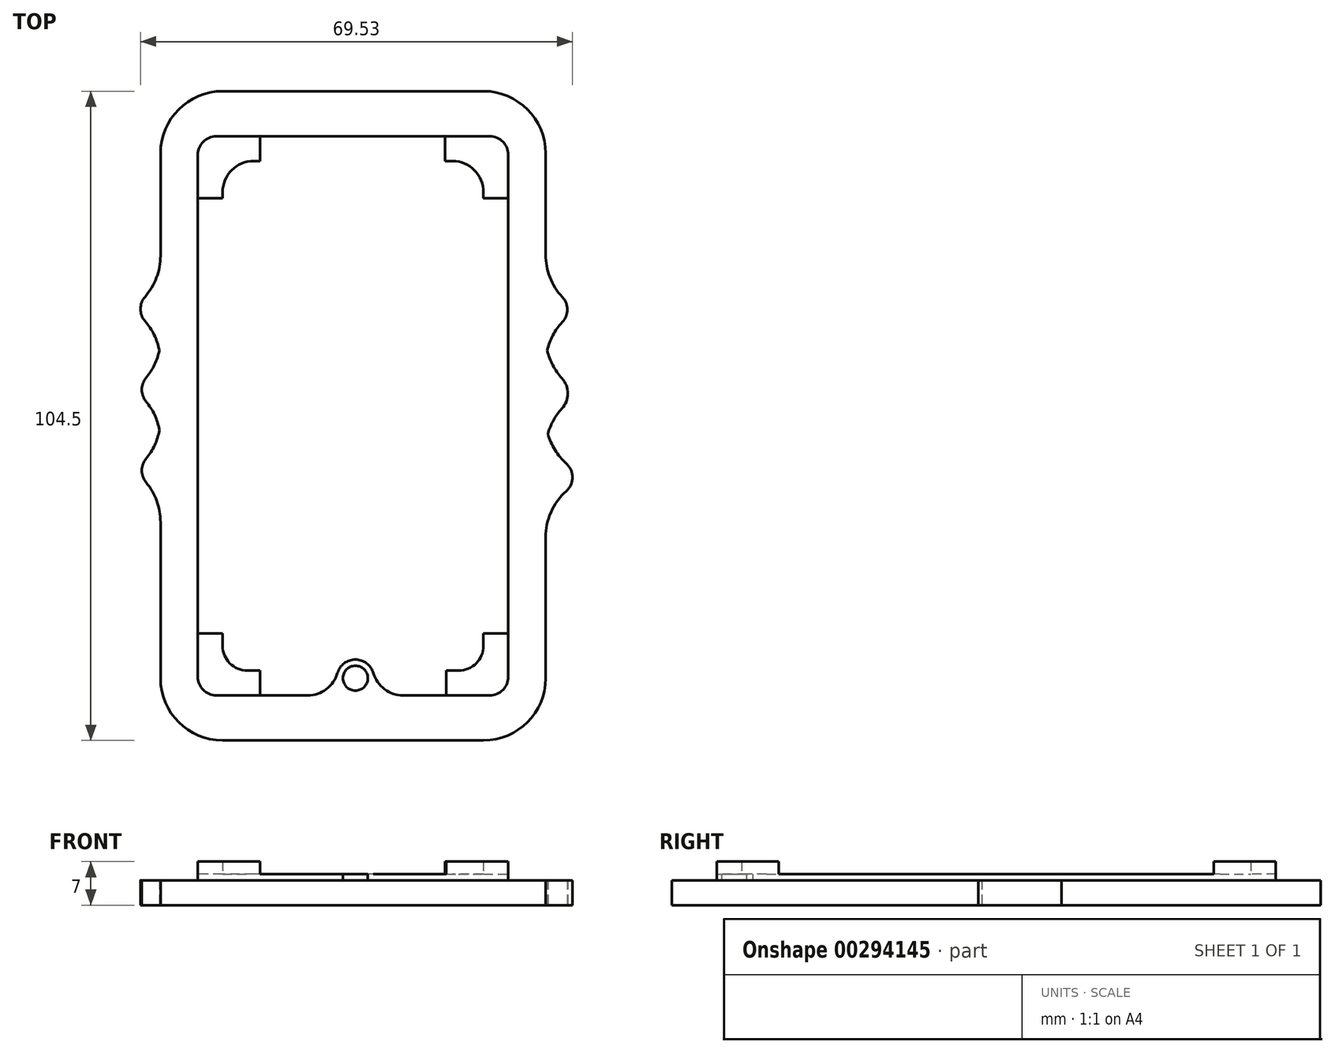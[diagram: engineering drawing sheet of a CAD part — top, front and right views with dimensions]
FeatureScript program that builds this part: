
annotation { "Feature Type Name" : "Feature", "Feature Type Description" : "" }
export const myFeature = defineFeature(function(context is Context, id is Id, definition is map)
    precondition{}
    {
        {
            var Q0;
            Q0=qCreatedBy(makeId("Top.planeOp"),FACE);
            var sketch = newSketch(context, id + "F0", { "sketchPlane" : qUnion([Q0])});
            skLineSegment(sketch, "E0.bottom", {"start": v(-9.13, 37.8) * mm, "end": v(20.7, 37.8) * mm});
            skLineSegment(sketch, "E0.top", {"start": v(-9.13, -52.2) * mm, "end": v(-1.43, -52.2) * mm});
            skLineSegment(sketch, "E0.left", {"start": v(-19.13, 27.8) * mm, "end": v(-19.13, -42.2) * mm});
            skLineSegment(sketch, "E0.right", {"start": v(30.87, 27.8) * mm, "end": v(30.87, -42.2) * mm});
            skPoint(sketch, "E1.end.orphan", {"position": v(5.87, -52.2) * mm});
            skPoint(sketch, "E1.start.orphan", {"position": v(5.87, 37.8) * mm});
            skPoint(sketch, "E2.visualSharp", {"position": v(30.87, 37.8) * mm});
            skPoint(sketch, "E3.visualSharp", {"position": v(-19.13, 37.8) * mm});
            skPoint(sketch, "E4.visualSharp", {"position": v(30.87, -52.2) * mm});
            skPoint(sketch, "E5.visualSharp", {"position": v(-19.13, -52.2) * mm});
            skArc(sketch, "E6", {"start": v(9.14, -48.6) * mm, "mid": v(6.25, -46.42) * mm, "end": v(3.37, -48.6) * mm});
            skLineSegment(sketch, "E7.trimOffspring", {"start": v(13.94, -52.2) * mm, "end": v(20.87, -52.2) * mm});
            skPoint(sketch, "E8", {"position": v(5.87, -46.45) * mm});
            skPoint(sketch, "E9.visualSharp", {"position": v(5.12, -52.2) * mm});
            skArc(sketch, "E9.filletArc", {"start": v(-1.43, -52.2) * mm, "mid": v(1.57, -51.2) * mm, "end": v(3.37, -48.6) * mm});
            skPoint(sketch, "E10.visualSharp", {"position": v(7.38, -52.2) * mm});
            skArc(sketch, "E10.filletArc", {"start": v(9.14, -48.6) * mm, "mid": v(10.93, -51.2) * mm, "end": v(13.94, -52.2) * mm});
            skPoint(sketch, "E11", {"position": v(-19.13, -7.2) * mm});
            skLineSegment(sketch, "E12.bottom", {"start": v(26.87, -59.45) * mm, "end": v(-15.13, -59.45) * mm});
            skLineSegment(sketch, "E12.top", {"start": v(26.87, 45.05) * mm, "end": v(-15.13, 45.05) * mm});
            skLineSegment(sketch, "E12.left", {"start": v(36.87, -49.45) * mm, "end": v(36.87, -26.78) * mm});
            skLineSegment(sketch, "E12.right", {"start": v(-25.13, -49.45) * mm, "end": v(-25.13, -24.3) * mm});
            skPoint(sketch, "E12.middle", {"position": v(5.87, -7.2) * mm});
            skPoint(sketch, "E13.visualSharp", {"position": v(-25.13, 45.05) * mm});
            skArc(sketch, "E13.filletArc", {"start": v(-15.13, 45.05) * mm, "mid": v(-22.2, 42.12) * mm, "end": v(-25.13, 35.05) * mm});
            skPoint(sketch, "E14.visualSharp", {"position": v(36.87, 45.05) * mm});
            skArc(sketch, "E14.filletArc", {"start": v(36.87, 35.05) * mm, "mid": v(33.95, 42.12) * mm, "end": v(26.87, 45.05) * mm});
            skPoint(sketch, "E15.visualSharp", {"position": v(36.87, -59.45) * mm});
            skArc(sketch, "E15.filletArc", {"start": v(26.87, -59.45) * mm, "mid": v(33.95, -56.52) * mm, "end": v(36.87, -49.45) * mm});
            skPoint(sketch, "E16.visualSharp", {"position": v(-25.13, -59.45) * mm});
            skArc(sketch, "E16.filletArc", {"start": v(-25.13, -49.45) * mm, "mid": v(-22.2, -56.52) * mm, "end": v(-15.13, -59.45) * mm});
            skPoint(sketch, "E17", {"position": v(30.87, -7.2) * mm});
            skPoint(sketch, "E18", {"position": v(36.87, -7.2) * mm});
            skPoint(sketch, "E19", {"position": v(-25.13, -7.2) * mm});
            skPoint(sketch, "E20", {"position": v(-25.13, 0) * mm});
            skPoint(sketch, "E21", {"position": v(36.87, 0) * mm});
            skLineSegment(sketch, "E22", {"start": v(36.87, 0) * mm, "end": v(36.87, 1.05) * mm});
            skArc(sketch, "E23", {"start": v(39.5, -6.04) * mm, "mid": v(40.45, -3.6) * mm, "end": v(39.5, -1.17) * mm});
            skArc(sketch, "E24", {"start": v(39.55, 7.86) * mm, "mid": v(40.35, 9.9) * mm, "end": v(39.55, 11.94) * mm});
            skLineSegment(sketch, "E25.trimOffspring", {"start": v(36.87, 5.6) * mm, "end": v(36.87, 6.94) * mm});
            skLineSegment(sketch, "E26.trimOffspring", {"start": v(36.87, 18.75) * mm, "end": v(36.87, 35.05) * mm});
            skPoint(sketch, "E27", {"position": v(40.35, 9.9) * mm});
            skPoint(sketch, "E28", {"position": v(40.45, -3.6) * mm});
            skPoint(sketch, "E29.visualSharp", {"position": v(36.87, 12.86) * mm});
            skArc(sketch, "E29.filletArc", {"start": v(36.87, 18.75) * mm, "mid": v(37.57, 15.1) * mm, "end": v(39.55, 11.94) * mm});
            skPoint(sketch, "E30.visualSharp", {"position": v(36.87, 6.94) * mm});
            skArc(sketch, "E30.filletArc", {"start": v(39.55, 7.86) * mm, "mid": v(37.57, 4.7) * mm, "end": v(36.87, 1.05) * mm});
            skArc(sketch, "E31.filletArc", {"start": v(36.87, 5.6) * mm, "mid": v(37.56, 1.97) * mm, "end": v(39.5, -1.17) * mm});
            skArc(sketch, "E32.filletArc", {"start": v(39.5, -6.04) * mm, "mid": v(37.56, -9.17) * mm, "end": v(36.87, -12.8) * mm});
            skLineSegment(sketch, "E33", {"start": v(36.87, -12.8) * mm, "end": v(36.87, -19.8) * mm});
            skArc(sketch, "E34", {"start": v(40.2, -19.33) * mm, "mid": v(41.2, -17.1) * mm, "end": v(40.2, -14.87) * mm});
            skLineSegment(sketch, "E35.trimOffspring", {"start": v(36.87, -12.8) * mm, "end": v(36.87, -7.43) * mm});
            skPoint(sketch, "E36", {"position": v(41.2, -17.1) * mm});
            skPoint(sketch, "E37.visualSharp", {"position": v(36.87, -19.8) * mm});
            skArc(sketch, "E37.filletArc", {"start": v(36.87, -7.43) * mm, "mid": v(37.74, -11.5) * mm, "end": v(40.2, -14.87) * mm});
            skArc(sketch, "E38.filletArc", {"start": v(40.2, -19.33) * mm, "mid": v(37.74, -22.7) * mm, "end": v(36.87, -26.78) * mm});
            skLineSegment(sketch, "E39", {"start": v(-25.13, 18.55) * mm, "end": v(-25.13, 19.98) * mm});
            skArc(sketch, "E40", {"start": v(-27.6, 11.97) * mm, "mid": v(-28.34, 10) * mm, "end": v(-27.6, 8.02) * mm});
            skLineSegment(sketch, "E41.trimOffspring", {"start": v(-25.13, 18.55) * mm, "end": v(-25.13, 35.05) * mm});
            skArc(sketch, "E42", {"start": v(-27.43, -1.08) * mm, "mid": v(-28.13, -3) * mm, "end": v(-27.43, -4.92) * mm});
            skArc(sketch, "E43", {"start": v(-27.43, -14.08) * mm, "mid": v(-28.13, -16) * mm, "end": v(-27.43, -17.92) * mm});
            skPoint(sketch, "E44.visualSharp", {"position": v(-25.13, -13) * mm});
            skArc(sketch, "E44.filletArc", {"start": v(-27.43, -14.08) * mm, "mid": v(-26.07, -11.93) * mm, "end": v(-25.3, -9.5) * mm});
            skPoint(sketch, "E45.visualSharp", {"position": v(-25.13, -19) * mm});
            skArc(sketch, "E45.filletArc", {"start": v(-25.13, -24.3) * mm, "mid": v(-25.72, -20.9) * mm, "end": v(-27.43, -17.92) * mm});
            skPoint(sketch, "E46.visualSharp", {"position": v(-25.13, -6) * mm});
            skArc(sketch, "E46.filletArc", {"start": v(-25.3, -9.5) * mm, "mid": v(-26.07, -7.07) * mm, "end": v(-27.43, -4.92) * mm});
            skArc(sketch, "E47.filletArc", {"start": v(-27.43, -1.08) * mm, "mid": v(-26.1, 1) * mm, "end": v(-25.32, 3.37) * mm});
            skPoint(sketch, "E48.visualSharp", {"position": v(-25.13, 7) * mm});
            skArc(sketch, "E48.filletArc", {"start": v(-25.32, 3.37) * mm, "mid": v(-26.15, 5.84) * mm, "end": v(-27.6, 8.02) * mm});
            skPoint(sketch, "E49.visualSharp", {"position": v(-25.13, 12.98) * mm});
            skArc(sketch, "E49.filletArc", {"start": v(-27.6, 11.97) * mm, "mid": v(-25.77, 15.04) * mm, "end": v(-25.13, 18.55) * mm});
            skCircle(sketch, "E50", {"center": v(6.25, -49.42) * mm, "radius": 2 * mm});
            skLineSegment(sketch, "E51", {"start": v(-19.13, 27.8) * mm, "end": v(-19.13, 34.8) * mm});
            skLineSegment(sketch, "E52", {"start": v(-16.13, 37.8) * mm, "end": v(-9.13, 37.8) * mm});
            skLineSegment(sketch, "E53", {"start": v(-9.13, 37.8) * mm, "end": v(-9.13, 33.8) * mm});
            skLineSegment(sketch, "E54", {"start": v(-9.13, 33.8) * mm, "end": v(-10.13, 33.8) * mm});
            skLineSegment(sketch, "E55", {"start": v(-15.13, 28.8) * mm, "end": v(-15.13, 27.8) * mm});
            skLineSegment(sketch, "E56", {"start": v(-15.13, 27.8) * mm, "end": v(-19.13, 27.8) * mm});
            skLineSegment(sketch, "E57", {"start": v(27.87, 37.8) * mm, "end": v(20.7, 37.8) * mm});
            skLineSegment(sketch, "E58", {"start": v(20.7, 33.8) * mm, "end": v(21.87, 33.8) * mm});
            skLineSegment(sketch, "E59", {"start": v(26.87, 28.8) * mm, "end": v(26.87, 27.8) * mm});
            skLineSegment(sketch, "E60", {"start": v(26.87, 27.8) * mm, "end": v(30.87, 27.8) * mm});
            skLineSegment(sketch, "E61", {"start": v(20.7, 37.8) * mm, "end": v(20.7, 33.8) * mm});
            skLineSegment(sketch, "E62", {"start": v(30.87, 34.8) * mm, "end": v(30.87, 27.8) * mm});
            skPoint(sketch, "E63.visualSharp", {"position": v(-15.13, 33.8) * mm});
            skArc(sketch, "E63.filletArc", {"start": v(-10.13, 33.8) * mm, "mid": v(-13.66, 32.33) * mm, "end": v(-15.13, 28.8) * mm});
            skPoint(sketch, "E64.visualSharp", {"position": v(26.87, 33.8) * mm});
            skArc(sketch, "E64.filletArc", {"start": v(26.87, 28.8) * mm, "mid": v(25.4, 32.33) * mm, "end": v(21.87, 33.8) * mm});
            skArc(sketch, "E65.filletArc", {"start": v(-16.13, 37.8) * mm, "mid": v(-18.25, 36.92) * mm, "end": v(-19.13, 34.8) * mm});
            skArc(sketch, "E66.filletArc", {"start": v(30.87, 34.8) * mm, "mid": v(30, 36.92) * mm, "end": v(27.87, 37.8) * mm});
            skLineSegment(sketch, "E67", {"start": v(30.87, -49.2) * mm, "end": v(30.87, -42.2) * mm});
            skLineSegment(sketch, "E68", {"start": v(30.87, -42.2) * mm, "end": v(26.87, -42.2) * mm});
            skLineSegment(sketch, "E69", {"start": v(26.87, -42.2) * mm, "end": v(26.87, -44.45) * mm});
            skLineSegment(sketch, "E70", {"start": v(27.87, -52.2) * mm, "end": v(20.87, -52.2) * mm});
            skPoint(sketch, "E4.filletArc.center.orphan", {"position": v(20.87, -42.2) * mm});
            skArc(sketch, "E71.filletArc", {"start": v(27.87, -52.2) * mm, "mid": v(30, -51.32) * mm, "end": v(30.87, -49.2) * mm});
            skLineSegment(sketch, "E72", {"start": v(-9.13, -52.2) * mm, "end": v(-16.13, -52.2) * mm});
            skLineSegment(sketch, "E73", {"start": v(-19.13, -49.2) * mm, "end": v(-19.13, -42.2) * mm});
            skPoint(sketch, "E74.end.orphan", {"position": v(20.87, -49.45) * mm});
            skLineSegment(sketch, "E75", {"start": v(20.87, -52.2) * mm, "end": v(20.87, -48.2) * mm});
            skLineSegment(sketch, "E76", {"start": v(20.87, -48.2) * mm, "end": v(22.87, -48.2) * mm});
            skLineSegment(sketch, "E77", {"start": v(26.87, -44.2) * mm, "end": v(26.87, -42.2) * mm});
            skPoint(sketch, "E78.visualSharp", {"position": v(26.87, -48.2) * mm});
            skArc(sketch, "E78.filletArc", {"start": v(22.87, -48.2) * mm, "mid": v(25.7, -47.03) * mm, "end": v(26.87, -44.2) * mm});
            skArc(sketch, "E79.filletArc", {"start": v(-19.13, -49.2) * mm, "mid": v(-18.25, -51.32) * mm, "end": v(-16.13, -52.2) * mm});
            skLineSegment(sketch, "E80", {"start": v(-9.13, -52.2) * mm, "end": v(-9.13, -48.2) * mm});
            skLineSegment(sketch, "E81", {"start": v(-9.13, -48.2) * mm, "end": v(-11.13, -48.2) * mm});
            skLineSegment(sketch, "E82", {"start": v(-15.13, -44.2) * mm, "end": v(-15.13, -42.2) * mm});
            skLineSegment(sketch, "E83", {"start": v(-15.13, -42.2) * mm, "end": v(-19.13, -42.2) * mm});
            skPoint(sketch, "E84.visualSharp", {"position": v(-15.13, -48.2) * mm});
            skArc(sketch, "E84.filletArc", {"start": v(-15.13, -44.2) * mm, "mid": v(-13.95, -47.03) * mm, "end": v(-11.13, -48.2) * mm});
            skSolve(sketch);
        }
        {
            var Q0;
            Q0=qSketchRegion(id+"F0",true);
            extrude(context, id + "F1", {"entities" : qUnion([Q0]), "depth" : 4 * mm});
        }
        {
            var Q0;
            Q0=makeQuery(id+"F0.imprint","IMPRINT",FACE,{"disambiguationData":[TD([[makeQuery(id+"F0.imprint","IMPRINT",EDGE,{"derivedFrom":sQuery(id+"F0.wireOp",EDGE,"E0.bottom")}),-1.0]])]});
            extrude(context, id + "F2", {"entities" : qUnion([Q0]), "operationType" : NewBodyOperationType.ADD, "depth" : 5 * mm});
        }
        {
            var Q0;
            Q0=makeQuery(id+"F0.imprint","IMPRINT",FACE,{"disambiguationData":[TD([[makeQuery(id+"F0.imprint","IMPRINT",EDGE,{"derivedFrom":sQuery(id+"F0.wireOp",EDGE,"E57")}),1.0]])]});
            var Q1;
            Q1=makeQuery(id+"F0.imprint","IMPRINT",FACE,{"disambiguationData":[TD([[makeQuery(id+"F0.imprint","IMPRINT",EDGE,{"derivedFrom":sQuery(id+"F0.wireOp",EDGE,"E51")}),-1.0]])]});
            var Q2;
            Q2=makeQuery(id+"F0.imprint","IMPRINT",FACE,{"disambiguationData":[TD([[makeQuery(id+"F0.imprint","IMPRINT",EDGE,{"derivedFrom":sQuery(id+"F0.wireOp",EDGE,"E67")}),1.0]])]});
            var Q3;
            Q3=makeQuery(id+"F0.imprint","IMPRINT",FACE,{"disambiguationData":[TD([[makeQuery(id+"F0.imprint","IMPRINT",EDGE,{"derivedFrom":sQuery(id+"F0.wireOp",EDGE,"E72")}),-1.0]])]});
            extrude(context, id + "F3", {"entities" : qUnion([Q0, Q1, Q2, Q3]), "operationType" : NewBodyOperationType.ADD, "depth" : 7 * mm});
        }
        {
            var Q0;
            Q0=makeQuery(id+"F0.imprint","IMPRINT",FACE,{"disambiguationData":[TD([[makeQuery(id+"F0.imprint","IMPRINT",EDGE,{"derivedFrom":sQuery(id+"F0.wireOp",EDGE,"E50")}),1.0]])]});
            extrude(context, id + "F4", {"entities" : qUnion([Q0]), "operationType" : NewBodyOperationType.ADD, "depth" : 5 * mm});
        }
    });
